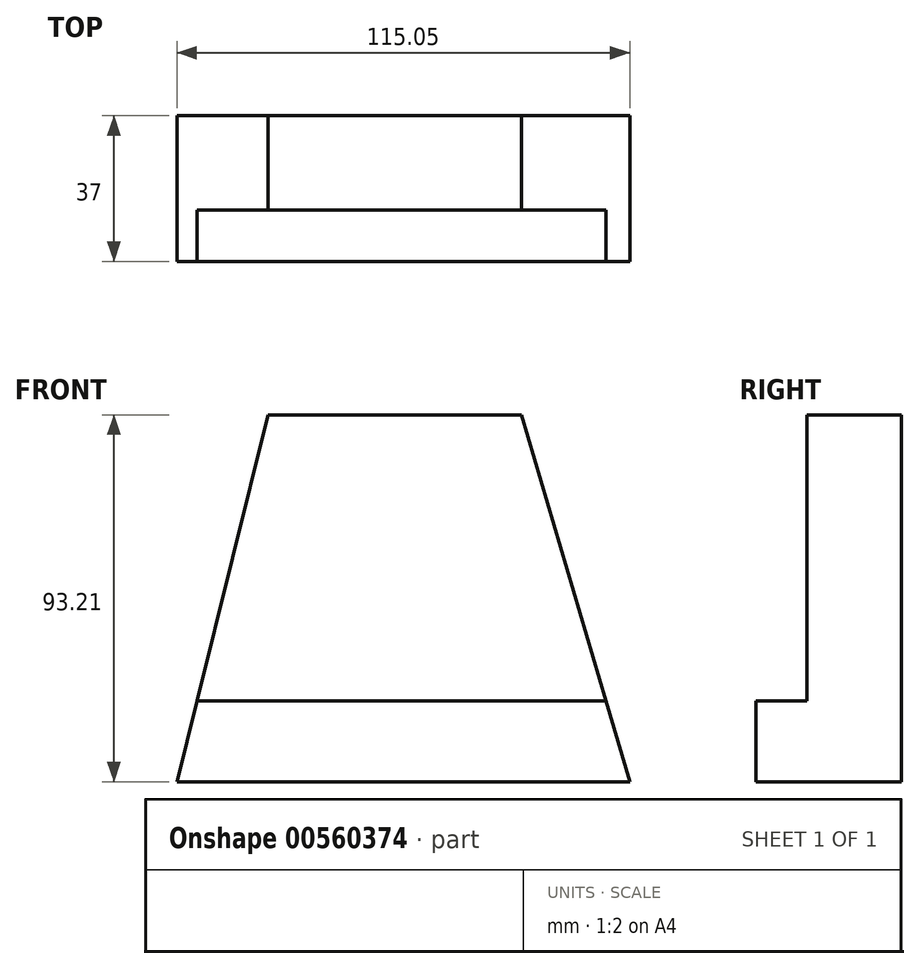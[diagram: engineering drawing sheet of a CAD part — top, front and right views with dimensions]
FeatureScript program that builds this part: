
annotation { "Feature Type Name" : "Feature", "Feature Type Description" : "" }
export const myFeature = defineFeature(function(context is Context, id is Id, definition is map)
    precondition{}
    {
        {
            var Q0;
            Q0=qCreatedBy(makeId("Front.planeOp"),FACE);
            var sketch = newSketch(context, id + "F0", { "sketchPlane" : qUnion([Q0])});
            skLineSegment(sketch, "E0", {"start": v(-33.76, 0) * mm, "end": v(30.52, 0) * mm});
            skLineSegment(sketch, "E1", {"start": v(30.52, 0) * mm, "end": v(58.07, -93.2) * mm});
            skLineSegment(sketch, "E2", {"start": v(58.07, -93.2) * mm, "end": v(-56.98, -93.2) * mm});
            skLineSegment(sketch, "E3", {"start": v(-56.98, -93.2) * mm, "end": v(-33.76, 0) * mm});
            skSolve(sketch);
        }
        {
            var Q0;
            Q0=makeQuery(id+"F0.imprint","IMPRINT",FACE,{"disambiguationData":[TD([[makeQuery(id+"F0.imprint","IMPRINT",EDGE,{"derivedFrom":sQuery(id+"F0.wireOp",EDGE,"E0")}),-1.0]])]});
            extrude(context, id + "F1", {"entities" : qUnion([Q0]), "depth" : 24 * mm, "offsetDistance" : 25 * mm});
        }
        {
            var Q0;
            Q0=makeQuery(id+"F1.opExtrude","CAP_FACE",FACE,{"disambiguationData":[OSD([sQuery(id+"F0.wireOp",EDGE,"E0"),sQuery(id+"F0.wireOp",EDGE,"E1"),sQuery(id+"F0.wireOp",EDGE,"E2"),sQuery(id+"F0.wireOp",EDGE,"E3")])],"isStart":false});
            var sketch = newSketch(context, id + "F2", { "sketchPlane" : qUnion([Q0])});
            skLineSegment(sketch, "E4", {"start": v(-56.98, -93.2) * mm, "end": v(58.07, -93.2) * mm});
            skLineSegment(sketch, "E5", {"start": v(58.07, -93.2) * mm, "end": v(52, -72.65) * mm});
            skLineSegment(sketch, "E6", {"start": v(52, -72.65) * mm, "end": v(-51.86, -72.65) * mm});
            skLineSegment(sketch, "E7", {"start": v(-51.86, -72.65) * mm, "end": v(-56.98, -93.2) * mm});
            skSolve(sketch);
        }
        {
            var Q0;
            Q0=makeQuery(id+"F2.imprint","IMPRINT",FACE,{"disambiguationData":[TD([[makeQuery(id+"F2.imprint","IMPRINT",EDGE,{"derivedFrom":sQuery(id+"F2.wireOp",EDGE,"E4")}),-1.0]])]});
            extrude(context, id + "F3", {"entities" : qUnion([Q0]), "operationType" : NewBodyOperationType.ADD, "depth" : 13 * mm, "offsetDistance" : 25 * mm});
        }
    });
